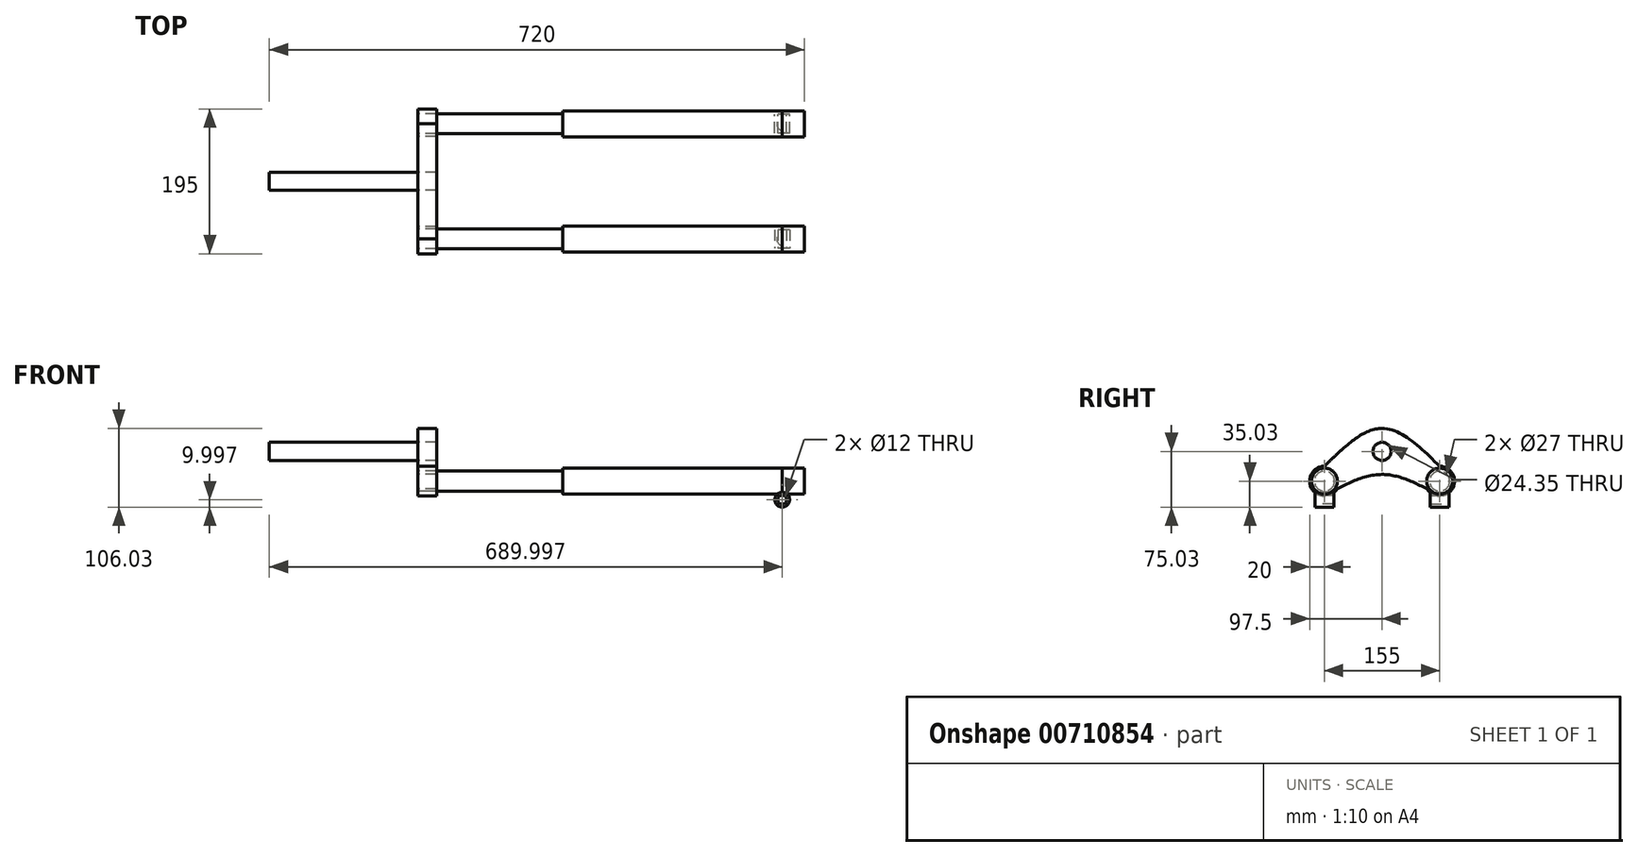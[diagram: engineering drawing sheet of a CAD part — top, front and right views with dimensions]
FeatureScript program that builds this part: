
annotation { "Feature Type Name" : "Feature", "Feature Type Description" : "" }
export const myFeature = defineFeature(function(context is Context, id is Id, definition is map)
    precondition{}
    {
        {
            var Q0;
            Q0=qCreatedBy(makeId("Right.planeOp"),FACE);
            var sketch = newSketch(context, id + "F0", { "sketchPlane" : qUnion([Q0])});
            skLineSegment(sketch, "E0", {"start": v(0, 0) * mm, "end": v(-77.5, 0) * mm, "construction": true});
            skLineSegment(sketch, "E1", {"start": v(0, 0) * mm, "end": v(77.5, 0) * mm, "construction": true});
            skLineSegment(sketch, "E2.0", {"start": v(0, 40) * mm, "end": v(77.5, 40) * mm, "construction": true});
            skLineSegment(sketch, "E2.1", {"start": v(0, 40) * mm, "end": v(-77.5, 40) * mm, "construction": true});
            skLineSegment(sketch, "E3", {"start": v(0, 0) * mm, "end": v(0, 40) * mm, "construction": true});
            skLineSegment(sketch, "E4.0", {"start": v(77.5, 0) * mm, "end": v(77.5, 40) * mm, "construction": true});
            skLineSegment(sketch, "E5.0", {"start": v(-77.5, 0) * mm, "end": v(-77.5, 40) * mm, "construction": true});
            skCircle(sketch, "E6", {"center": v(-77.5, 0) * mm, "radius": 13.5 * mm});
            skCircle(sketch, "E7", {"center": v(77.5, 0) * mm, "radius": 13.5 * mm});
            skCircle(sketch, "E8", {"center": v(77.5, 0) * mm, "radius": 20 * mm});
            skCircle(sketch, "E9", {"center": v(-77.5, 0) * mm, "radius": 20 * mm});
            skCircle(sketch, "E10", {"center": v(0, 40) * mm, "radius": 12.18 * mm});
            skCircle(sketch, "E11", {"center": v(0, 40) * mm, "radius": 31 * mm});
            skLineSegment(sketch, "E12.MirrorCS", {"start": v(77.5, 0) * mm, "end": v(77.5, -40) * mm, "construction": true});
            skLineSegment(sketch, "E13.MirrorCS", {"start": v(-77.5, 0) * mm, "end": v(-77.5, -40) * mm, "construction": true});
            skLineSegment(sketch, "E14.0", {"start": v(5, 45) * mm, "end": v(-77.5, 45) * mm});
            skLineSegment(sketch, "E14.1", {"start": v(5, 0) * mm, "end": v(5, 45) * mm});
            skLineSegment(sketch, "E15", {"start": v(0, 40) * mm, "end": v(0, 74.35) * mm, "construction": true});
            skPoint(sketch, "E16", {"position": v(0, 71) * mm});
            skPoint(sketch, "E17", {"position": v(77.5, 20) * mm});
            skPoint(sketch, "E18", {"position": v(-77.5, 20) * mm});
            skFitSpline(sketch, "E19", {"points": [v(77.5, 20) * mm, v(0, 71) * mm, v(-77.5, 20) * mm], "startDerivative": vector(-155, 153) * mm, "endDerivative": vector(-155, -153) * mm});
            skPoint(sketch, "E20", {"position": v(77.5, -20) * mm});
            skPoint(sketch, "E21", {"position": v(0, 9) * mm});
            skPoint(sketch, "E22", {"position": v(-77.5, -20) * mm});
            skFitSpline(sketch, "E23", {"points": [v(77.5, -20) * mm, v(0, 9) * mm, v(-77.5, -20) * mm], "startDerivative": vector(-155, 87) * mm, "endDerivative": vector(-155, -87) * mm});
            skSolve(sketch);
        }
        {
            var Q0;
            Q0=makeQuery(id+"F0.imprint","IMPRINT",FACE,{"disambiguationData":[TD([[makeQuery(id+"F0.imprint","IMPRINT",EDGE,{"derivedFrom":sQuery(id+"F0.wireOp",EDGE,"E7")}),1.0]])]});
            var Q1;
            Q1=makeQuery(id+"F0.imprint","IMPRINT",FACE,{"disambiguationData":[TD([[makeQuery(id+"F0.imprint","IMPRINT",EDGE,{"derivedFrom":sQuery(id+"F0.wireOp",EDGE,"E6")}),1.0]])]});
            extrude(context, id + "F1", {"entities" : qUnion([Q0, Q1]), "depth" : 195 * mm, "offsetDistance" : 25 * mm});
        }
        {
            var Q0;
            Q0=qSketchRegion(id+"F0",true);
            extrude(context, id + "F2", {"entities" : qUnion([Q0]), "depth" : 25 * mm, "offsetDistance" : 25 * mm});
        }
        {
            var Q0;
            {var subQ0=sQuery(id+"F0.wireOp",EDGE,"E14.0");var subQ1=sQuery(id+"F0.wireOp",EDGE,"E10");var subQ2=makeQuery(id+"F0.imprint","INTERSECT",VERTEX,{"derivedFrom":[subQ1,subQ0]});Q0=makeQuery(id+"F0.imprint","IMPRINT",FACE,{"disambiguationData":[TD([[makeQuery(id+"F0.imprint","IMPRINT",EDGE,{"disambiguationData":[TD([[subQ2,-1.0]])],"derivedFrom":subQ1}),1.0]])]});}
            var Q1;
            {var subQ0=sQuery(id+"F0.wireOp",EDGE,"E14.0");var subQ1=sQuery(id+"F0.wireOp",EDGE,"E10");var subQ2=makeQuery(id+"F0.imprint","INTERSECT",VERTEX,{"derivedFrom":[subQ1,subQ0]});Q1=makeQuery(id+"F0.imprint","IMPRINT",FACE,{"disambiguationData":[TD([[makeQuery(id+"F0.imprint","IMPRINT",EDGE,{"disambiguationData":[TD([[subQ2,1.0]])],"derivedFrom":subQ1}),1.0]])]});}
            extrude(context, id + "F3", {"entities" : qUnion([Q0, Q1]), "oppositeDirection" : true, "depth" : 200 * mm, "offsetDistance" : 25 * mm});
        }
        {
            var Q0;
            Q0=makeQuery(id+"F1.opExtrude","CAP_FACE",FACE,{"disambiguationData":[OSD([sQuery(id+"F0.wireOp",EDGE,"E7")])],"isStart":false});
            var sketch = newSketch(context, id + "F4", { "sketchPlane" : qUnion([Q0])});
            skCircle(sketch, "E24", {"center": v(77.5, 0) * mm, "radius": 17.5 * mm});
            skSolve(sketch);
        }
        {
            var Q0;
            Q0=makeQuery(id+"F1.opExtrude","CAP_FACE",FACE,{"disambiguationData":[OSD([sQuery(id+"F0.wireOp",EDGE,"E6")])],"isStart":false});
            var sketch = newSketch(context, id + "F5", { "sketchPlane" : qUnion([Q0])});
            skCircle(sketch, "E25", {"center": v(-77.5, 0) * mm, "radius": 17.5 * mm});
            skSolve(sketch);
        }
        {
            var Q0;
            Q0=makeQuery(id+"F3.opExtrude","CAP_FACE",FACE,{"disambiguationData":[OSD([sQuery(id+"F0.wireOp",EDGE,"E10")])],"isStart":true});
            extrude(context, id + "F6", {"entities" : qUnion([Q0]), "depth" : 25 * mm, "offsetDistance" : 25 * mm});
        }
        {
            var Q0;
            Q0=makeQuery(id+"F5.imprint","IMPRINT",FACE,{"disambiguationData":[TD([[makeQuery(id+"F5.imprint","IMPRINT",EDGE,{"derivedFrom":sQuery(id+"F5.wireOp",EDGE,"E25")}),1.0]])]});
            var Q1;
            Q1=makeQuery(id+"F4.imprint","IMPRINT",FACE,{"disambiguationData":[TD([[makeQuery(id+"F4.imprint","IMPRINT",EDGE,{"derivedFrom":sQuery(id+"F4.wireOp",EDGE,"E24")}),1.0]])]});
            var Q2;
            Q2=makeQuery(id+"F5.imprint","IMPRINT",FACE,{"disambiguationData":[TD([[makeQuery(id+"F5.imprint","IMPRINT",EDGE,{"derivedFrom":makeQuery(id+"F1.opExtrude","CAP_EDGE",EDGE,{"disambiguationData":[OSD([sQuery(id+"F0.wireOp",EDGE,"E6")])],"isStart":false})}),1.0]])]});
            var Q3;
            Q3=makeQuery(id+"F4.imprint","IMPRINT",FACE,{"disambiguationData":[TD([[makeQuery(id+"F4.imprint","IMPRINT",EDGE,{"derivedFrom":makeQuery(id+"F1.opExtrude","CAP_EDGE",EDGE,{"disambiguationData":[OSD([sQuery(id+"F0.wireOp",EDGE,"E7")])],"isStart":false})}),1.0]])]});
            extrude(context, id + "F7", {"entities" : qUnion([Q0, Q1, Q2, Q3]), "depth" : 295 * mm, "offsetDistance" : 25 * mm});
        }
        {
            var Q0;
            Q0=makeQuery(id+"F7.opExtrude","CAP_FACE",FACE,{"disambiguationData":[OSD([sQuery(id+"F5.wireOp",EDGE,"E25")])],"isStart":false});
            var sketch = newSketch(context, id + "F8", { "sketchPlane" : qUnion([Q0])});
            skLineSegment(sketch, "E26", {"start": v(109.4, 0) * mm, "end": v(-105.9, 0) * mm, "construction": true});
            skLineSegment(sketch, "E27.0", {"start": v(78.55, -17.5) * mm, "end": v(-77.5, -17.5) * mm, "construction": true});
            skArc(sketch, "E28.0", {"start": v(32.34, -46.42) * mm, "mid": v(132.3, -34.52) * mm, "end": v(99.87, 60.78) * mm, "construction": true});
            skFitSpline(sketch, "E28.1", {"points": [v(-55.59, -59.04) * mm, v(-52.36, -57.22) * mm, v(-46.07, -53.7) * mm, v(-37.18, -48.87) * mm, v(-28.88, -44.65) * mm, v(-21.25, -41.18) * mm, v(-15.56, -39) * mm, v(-11.47, -37.7) * mm, v(-8.66, -36.93) * mm, v(-6.1, -36.38) * mm, v(-4.19, -36.07) * mm, v(-2.79, -35.9) * mm, v(-1.8, -35.82) * mm, v(-1.02, -35.78) * mm, v(-0.43, -35.77) * mm, v(0, -35.76) * mm, v(0.43, -35.77) * mm, v(1.02, -35.78) * mm, v(1.8, -35.82) * mm, v(2.79, -35.9) * mm, v(4.19, -36.07) * mm, v(6.1, -36.38) * mm, v(8.66, -36.93) * mm, v(11.47, -37.7) * mm, v(15.56, -39) * mm, v(21.25, -41.18) * mm, v(28.88, -44.65) * mm, v(37.18, -48.87) * mm, v(46.07, -53.7) * mm, v(52.36, -57.22) * mm, v(55.59, -59.04) * mm], "construction": true});
            skArc(sketch, "E28.2", {"start": v(-99.87, 60.78) * mm, "mid": v(-132.3, -34.52) * mm, "end": v(-32.34, -46.42) * mm, "construction": true});
            skFitSpline(sketch, "E28.3", {"points": [v(108.95, 51.86) * mm, v(105.72, 55.05) * mm, v(99.1, 61.58) * mm, v(88.64, 71.6) * mm, v(77.54, 81.54) * mm, v(67.58, 89.55) * mm, v(59, 95.64) * mm, v(52.21, 100) * mm, v(44.97, 104.08) * mm, v(37.22, 107.8) * mm, v(30.27, 110.5) * mm, v(24.38, 112.32) * mm, v(19.8, 113.5) * mm, v(15.07, 114.47) * mm, v(11, 115.08) * mm, v(7.67, 115.43) * mm, v(5.14, 115.62) * mm, v(3.01, 115.72) * mm, v(1.3, 115.76) * mm, v(0, 115.77) * mm, v(-1.3, 115.76) * mm, v(-3.01, 115.72) * mm, v(-5.14, 115.62) * mm, v(-7.67, 115.43) * mm, v(-11, 115.08) * mm, v(-15.07, 114.47) * mm, v(-19.8, 113.5) * mm, v(-24.38, 112.32) * mm, v(-30.27, 110.5) * mm, v(-37.22, 107.8) * mm, v(-44.97, 104.08) * mm, v(-52.21, 100) * mm, v(-59, 95.64) * mm, v(-67.58, 89.55) * mm, v(-77.54, 81.54) * mm, v(-88.64, 71.6) * mm, v(-99.1, 61.58) * mm, v(-105.72, 55.05) * mm, v(-108.95, 51.86) * mm], "construction": true});
            skPoint(sketch, "E29.orphan", {"position": v(78.55, 0) * mm});
            skLineSegment(sketch, "E30.0", {"start": v(109.4, 30) * mm, "end": v(-105.9, 30) * mm, "construction": true});
            skSolve(sketch);
        }
        {
            var Q0;
            Q0=makeQuery(id+"F7.opExtrude","CAP_FACE",FACE,{"disambiguationData":[OSD([sQuery(id+"F4.wireOp",EDGE,"E24")])],"isStart":false});
            var sketch = newSketch(context, id + "F9", { "sketchPlane" : qUnion([Q0])});
            skCircle(sketch, "E31", {"center": v(77.5, 0) * mm, "radius": 25 * mm});
            skCircle(sketch, "E32", {"center": v(-77.43, 0) * mm, "radius": 25 * mm});
            skLineSegment(sketch, "E33", {"start": v(-77.43, 0) * mm, "end": v(-77.43, -25) * mm, "construction": true});
            skLineSegment(sketch, "E34", {"start": v(77.5, 0) * mm, "end": v(77.5, -25) * mm, "construction": true});
            skSolve(sketch);
        }
        {
            var Q0;
            Q0=sQuery(id+"F9.wireOp",EDGE,"E34");
            cPlane(context, id + "F10", {"entities" : qUnion([Q0]), "cplaneType" : CPlaneType.LINE_ANGLE, "offset" : 25 * mm, "angle" : 270 * degree, "width" : 150 * mm, "height" : 150 * mm});
        }
        {
            var Q0;
            Q0=qCreatedBy(id+"F10.planeOp",FACE);
            var sketch = newSketch(context, id + "F11", { "sketchPlane" : qUnion([Q0])});
            skCircle(sketch, "E35", {"center": v(490, -25.03) * mm, "radius": 6 * mm});
            skCircle(sketch, "E36", {"center": v(490, -25.03) * mm, "radius": 10 * mm});
            skSolve(sketch);
        }
        {
            var Q0;
            Q0=makeQuery(id+"F11.imprint","IMPRINT",FACE,{"disambiguationData":[TD([[makeQuery(id+"F11.imprint","IMPRINT",EDGE,{"derivedFrom":sQuery(id+"F11.wireOp",EDGE,"E35")}),-1.0]])]});
            extrude(context, id + "F12", {"entities" : qUnion([Q0]), "depth" : 12.5 * mm, "offsetDistance" : 25 * mm});
        }
        {
            var Q0;
            Q0=makeQuery(id+"F12.opExtrude","CAP_FACE",FACE,{"disambiguationData":[OSD([sQuery(id+"F11.wireOp",EDGE,"E35"),sQuery(id+"F11.wireOp",EDGE,"E36")])],"isStart":true});
            extrude(context, id + "F13", {"entities" : qUnion([Q0]), "depth" : 12.5 * mm, "offsetDistance" : 25 * mm});
        }
        {
            var Q0;
            Q0=makeQuery(id+"F13.opExtrude","SWEPT_BODY",BODY,{"disambiguationData":[OSD([sQuery(id+"F11.wireOp",EDGE,"E35"),sQuery(id+"F11.wireOp",EDGE,"E36")])]});
            var Q1;
            Q1=makeQuery(id+"F12.opExtrude","SWEPT_BODY",BODY,{"disambiguationData":[OSD([sQuery(id+"F11.wireOp",EDGE,"E35"),sQuery(id+"F11.wireOp",EDGE,"E36")])]});
            var Q2;
            Q2=qCreatedBy(makeId("Front.planeOp"),FACE);
            mirror(context, id + "F14", {"operationType" : NewBodyOperationType.ADD, "entities" : qUnion([Q0, Q1]), "mirrorPlane" : qUnion([Q2])});
        }
        {
            var Q0;
            Q0=makeQuery(id+"F9.imprint","IMPRINT",FACE,{"disambiguationData":[TD([[makeQuery(id+"F9.imprint","IMPRINT",EDGE,{"derivedFrom":makeQuery(id+"F7.opExtrude","CAP_EDGE",EDGE,{"disambiguationData":[OSD([sQuery(id+"F4.wireOp",EDGE,"E24")])],"isStart":false})}),1.0]])]});
            var Q1;
            Q1=makeQuery(id+"F8.imprint","IMPRINT",FACE,{"disambiguationData":[TD([[makeQuery(id+"F8.imprint","IMPRINT",EDGE,{"derivedFrom":makeQuery(id+"F7.opExtrude","CAP_EDGE",EDGE,{"disambiguationData":[OSD([sQuery(id+"F5.wireOp",EDGE,"E25")])],"isStart":false})}),1.0]])]});
            extrude(context, id + "F15", {"entities" : qUnion([Q0, Q1]), "depth" : 30 * mm, "offsetDistance" : 25 * mm});
        }
    });
